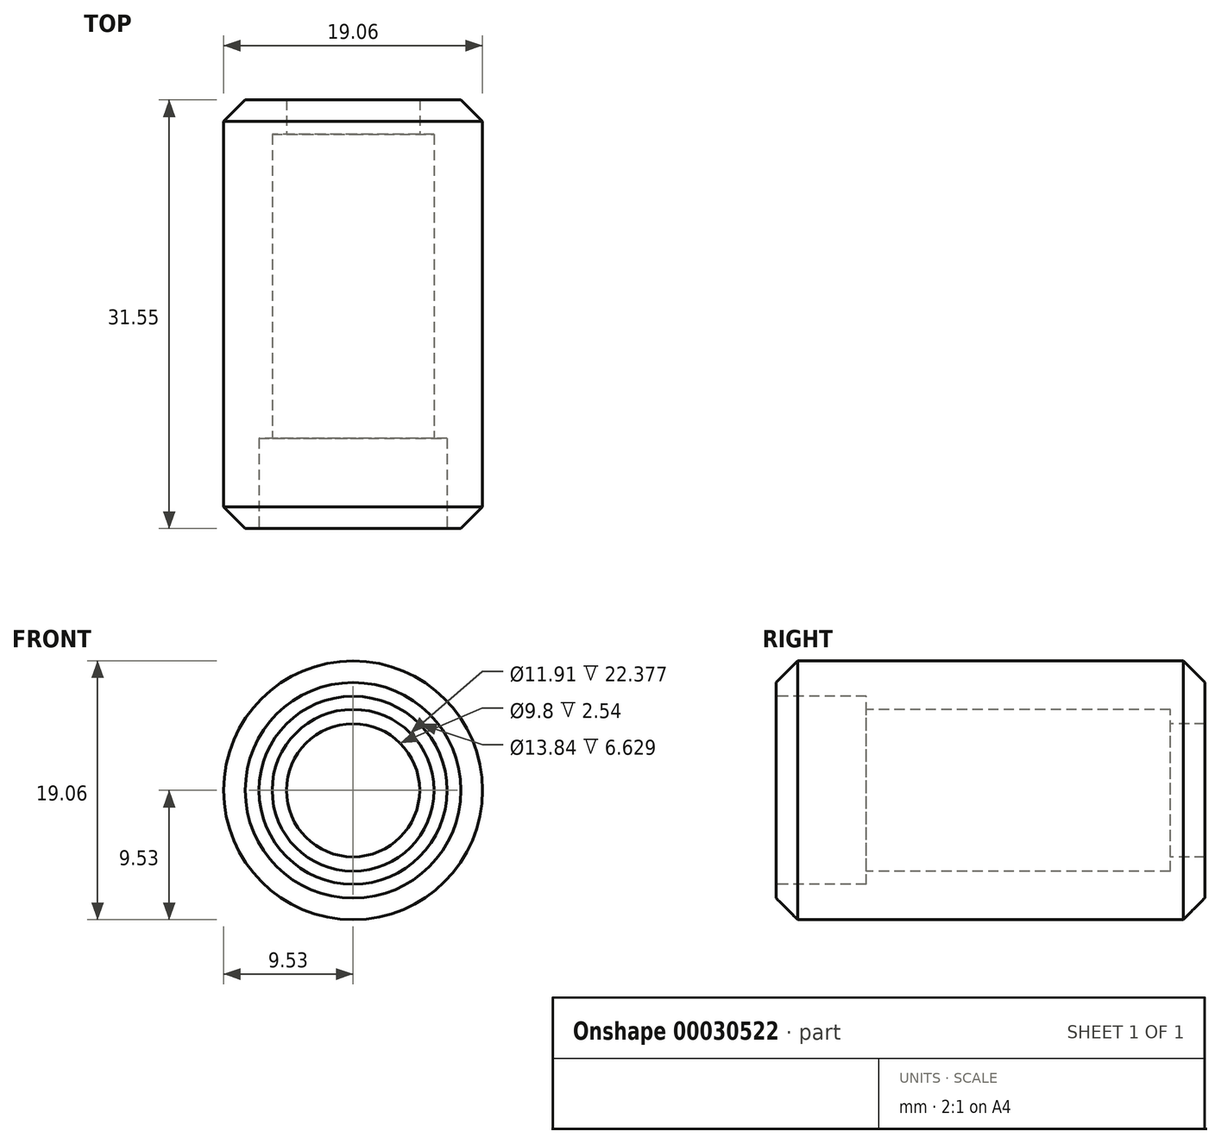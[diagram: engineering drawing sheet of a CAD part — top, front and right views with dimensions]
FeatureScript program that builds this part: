
annotation { "Feature Type Name" : "Feature", "Feature Type Description" : "" }
export const myFeature = defineFeature(function(context is Context, id is Id, definition is map)
    precondition{}
    {
        {
            var Q0;
            Q0=qCreatedBy(makeId("Front.planeOp"),FACE);
            var sketch = newSketch(context, id + "F0", { "sketchPlane" : qUnion([Q0])});
            skCircle(sketch, "E0", {"center": v(0, 0) * mm, "radius": 9.53 * mm});
            skSolve(sketch);
        }
        {
            var Q0;
            Q0 = qSketchRegion(id + "F0", true);
            extrude(context, id + "F1", {"entities" : qUnion([Q0]), "depth" : 31.55 * mm});
        }
        {
            var Q0;
            Q0=makeQuery(id+"F1.opExtrude","CAP_FACE",FACE,{"disambiguationData":[OSD([sQuery(id+"F0.wireOp",EDGE,"E0")])],"isStart":false});
            var sketch = newSketch(context, id + "F2", { "sketchPlane" : qUnion([Q0])});
            skPoint(sketch, "E1", {"position": v(0, 0) * mm});
            skSolve(sketch);
        }
        {
            var Q0;
            Q0=sQuery(id+"F2.wireOp",VERTEX,"E1");
            var Q1;
            Q1=makeQuery(id+"F1.opExtrude","SWEPT_BODY",BODY,{"disambiguationData":[OSD([sQuery(id+"F0.wireOp",EDGE,"E0")])]});
            hole(context, id + "F3", {"style" : HoleStyle.C_BORE, "holeDiameter" : 9.8 * mm, "cBoreDiameter" : 11.9 * mm, "cBoreDepth" : 29 * mm, "endStyle" : HoleEndStyle.THROUGH, "locations" : qUnion([Q0]), "scope" : qUnion([Q1])});
        }
        {
            var Q0;
            Q0=makeQuery(id+"F1.opExtrude","CAP_FACE",FACE,{"disambiguationData":[OSD([sQuery(id+"F0.wireOp",EDGE,"E0")])],"isStart":false});
            var sketch = newSketch(context, id + "F4", { "sketchPlane" : qUnion([Q0])});
            skCircle(sketch, "E2", {"center": v(0, 0) * mm, "radius": 6.92 * mm});
            skSolve(sketch);
        }
        {
            var Q0;
            Q0 = qSketchRegion(id + "F4", true);
            extrude(context, id + "F5", {"entities" : qUnion([Q0]), "operationType" : NewBodyOperationType.REMOVE, "oppositeDirection" : true, "depth" : 6.63 * mm});
        }
        {
            var Q0;
            Q0=makeQuery(id+"F1.opExtrude","CAP_EDGE",EDGE,{"disambiguationData":[OSD([sQuery(id+"F0.wireOp",EDGE,"E0")])],"isStart":false});
            var Q1;
            Q1=makeQuery(id+"F1.opExtrude","CAP_EDGE",EDGE,{"disambiguationData":[OSD([sQuery(id+"F0.wireOp",EDGE,"E0")])],"isStart":true});
            chamfer(context, id + "F6", {"entities" : qUnion([Q0, Q1]), "chamferType" : ChamferType.OFFSET_ANGLE, "width" : 1.59 * mm, "oppositeDirection" : false, "angle" : 45 * degree, "tangentPropagation" : true});
        }
    });
